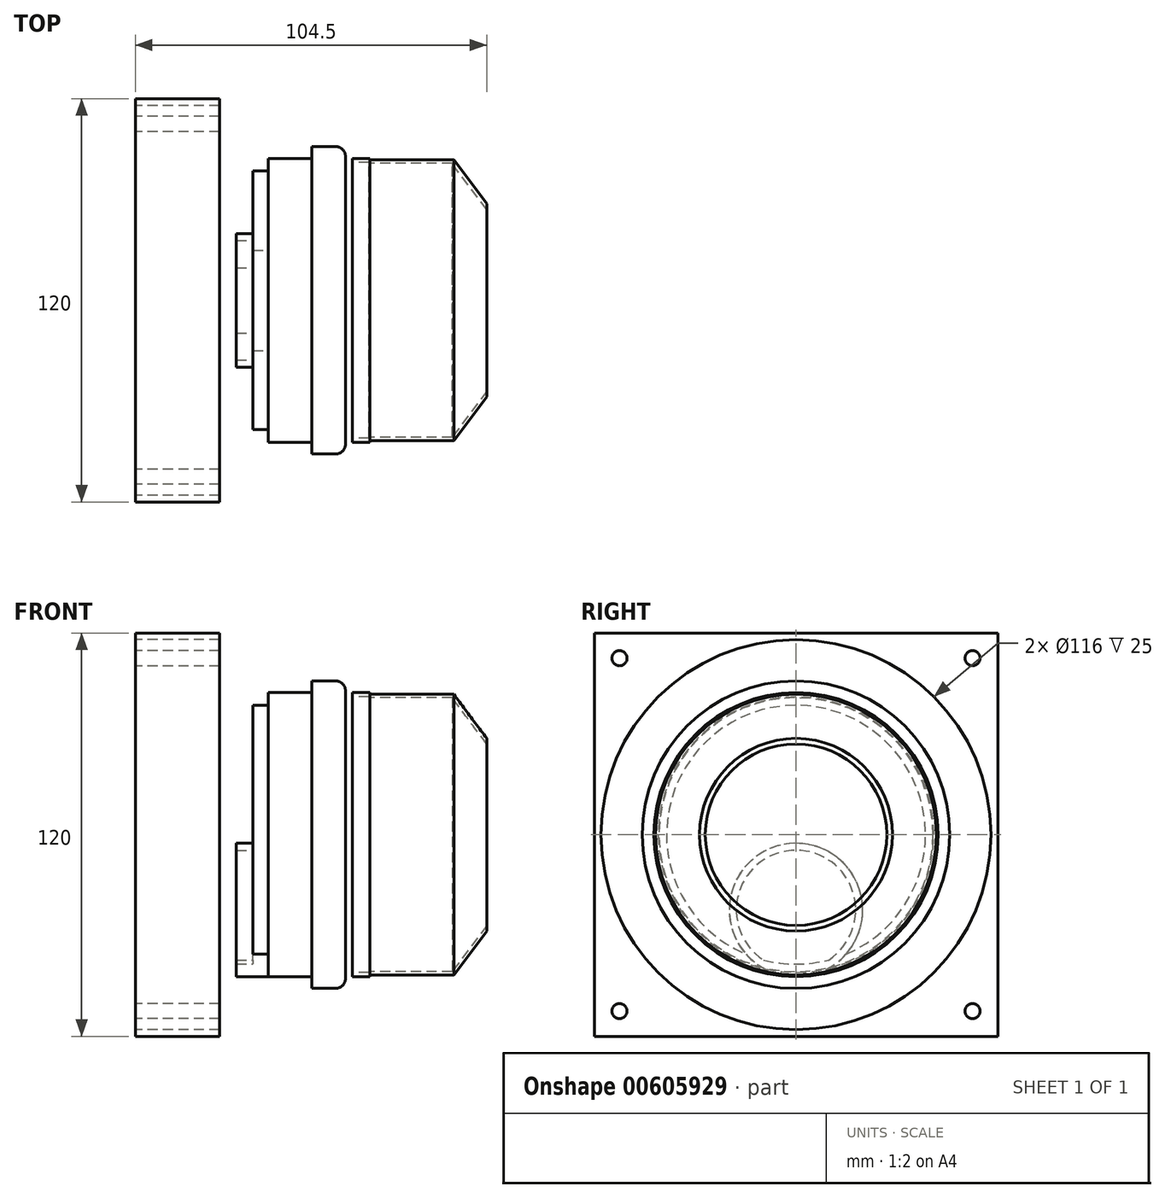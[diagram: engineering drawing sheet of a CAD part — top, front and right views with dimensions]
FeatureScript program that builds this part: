
annotation { "Feature Type Name" : "Feature", "Feature Type Description" : "" }
export const myFeature = defineFeature(function(context is Context, id is Id, definition is map)
    precondition{}
    {
        {
            var Q0;
            Q0=qCreatedBy(makeId("Top.planeOp"),FACE);
            var sketch = newSketch(context, id + "F0", { "sketchPlane" : qUnion([Q0])});
            skLineSegment(sketch, "E0.bottom", {"start": v(12.5, -60) * mm, "end": v(-12.5, -60) * mm});
            skLineSegment(sketch, "E0.top", {"start": v(12.5, 60) * mm, "end": v(-12.5, 60) * mm});
            skLineSegment(sketch, "E0.left", {"start": v(12.5, -60) * mm, "end": v(12.5, 60) * mm});
            skLineSegment(sketch, "E0.right", {"start": v(-12.5, -60) * mm, "end": v(-12.5, 60) * mm});
            skPoint(sketch, "E0.middle", {"position": v(0, 0) * mm});
            skLineSegment(sketch, "E1.bottom", {"start": v(50, -45.75) * mm, "end": v(40, -45.75) * mm});
            skLineSegment(sketch, "E1.top", {"start": v(50, 45.75) * mm, "end": v(40, 45.75) * mm});
            skLineSegment(sketch, "E1.left", {"start": v(50, -45.75) * mm, "end": v(50, 45.75) * mm});
            skLineSegment(sketch, "E1.right", {"start": v(40, -45.75) * mm, "end": v(40, 45.75) * mm});
            skPoint(sketch, "E1.middle", {"position": v(45, 0) * mm});
            skPoint(sketch, "E1.middle.positionSnap0", {"position": v(12.5, 0) * mm});
            skPoint(sketch, "E1.centerSnap0", {"position": v(12.5, 0) * mm});
            skLineSegment(sketch, "E2", {"start": v(-151.33, 0) * mm, "end": v(194.4, 0) * mm});
            skLineSegment(sketch, "E3", {"start": v(40, 42.25) * mm, "end": v(27, 42.25) * mm});
            skLineSegment(sketch, "E4", {"start": v(27, 42.25) * mm, "end": v(27, 0) * mm});
            skLineSegment(sketch, "E5.MirrorCS", {"start": v(27, -42.25) * mm, "end": v(27, 0) * mm});
            skLineSegment(sketch, "E6.MirrorCS", {"start": v(40, -42.25) * mm, "end": v(27, -42.25) * mm});
            skLineSegment(sketch, "E7", {"start": v(27, 38.5) * mm, "end": v(22.5, 38.5) * mm});
            skLineSegment(sketch, "E8", {"start": v(22.5, 38.5) * mm, "end": v(22.5, 0) * mm});
            skLineSegment(sketch, "E9.MirrorCS", {"start": v(22.5, -38.5) * mm, "end": v(22.5, 0) * mm});
            skLineSegment(sketch, "E10.MirrorCS", {"start": v(27, -38.5) * mm, "end": v(22.5, -38.5) * mm});
            skLineSegment(sketch, "E11.bottom", {"start": v(57, -41) * mm, "end": v(52, -41) * mm});
            skLineSegment(sketch, "E11.top", {"start": v(57, 41) * mm, "end": v(52, 41) * mm});
            skLineSegment(sketch, "E11.left", {"start": v(57, -41) * mm, "end": v(57, 41) * mm});
            skLineSegment(sketch, "E11.right", {"start": v(52, -41) * mm, "end": v(52, 41) * mm});
            skPoint(sketch, "E11.middle", {"position": v(54.5, 0) * mm});
            skLineSegment(sketch, "E12", {"start": v(52, -41) * mm, "end": v(52, -42.25) * mm});
            skLineSegment(sketch, "E13", {"start": v(52, -42.25) * mm, "end": v(57.2, -42.25) * mm});
            skLineSegment(sketch, "E14", {"start": v(57.2, -42.25) * mm, "end": v(57.2, -41.75) * mm});
            skLineSegment(sketch, "E15", {"start": v(57.2, -41.75) * mm, "end": v(82.2, -41.75) * mm});
            skLineSegment(sketch, "E16", {"start": v(82.2, -41.75) * mm, "end": v(92, -28.67) * mm});
            skLineSegment(sketch, "E17", {"start": v(92, -28.67) * mm, "end": v(92, -27) * mm});
            skLineSegment(sketch, "E18", {"start": v(92, -27) * mm, "end": v(81.7, -40.75) * mm});
            skLineSegment(sketch, "E19", {"start": v(81.7, -40.75) * mm, "end": v(57, -40.75) * mm});
            skLineSegment(sketch, "E20.MirrorCS", {"start": v(52, 41) * mm, "end": v(52, 42.25) * mm});
            skLineSegment(sketch, "E21.MirrorCS", {"start": v(52, 42.25) * mm, "end": v(57.2, 42.25) * mm});
            skLineSegment(sketch, "E22.MirrorCS", {"start": v(81.7, 40.75) * mm, "end": v(57, 40.75) * mm});
            skLineSegment(sketch, "E23.MirrorCS", {"start": v(57.2, 42.25) * mm, "end": v(57.2, 41.75) * mm});
            skLineSegment(sketch, "E24.MirrorCS", {"start": v(57.2, 41.75) * mm, "end": v(82.2, 41.75) * mm});
            skLineSegment(sketch, "E25.MirrorCS", {"start": v(92, 27) * mm, "end": v(81.7, 40.75) * mm});
            skLineSegment(sketch, "E26.MirrorCS", {"start": v(82.2, 41.75) * mm, "end": v(92, 28.67) * mm});
            skLineSegment(sketch, "E27.MirrorCS", {"start": v(92, 28.67) * mm, "end": v(92, 27) * mm});
            skSolve(sketch);
        }
        {
            var Q0;
            {var subQ0=sQuery(id+"F0.wireOp",EDGE,"E0.top");Q0=makeQuery(id+"F0.imprint","IMPRINT",FACE,{"disambiguationData":[TD([[makeQuery(id+"F0.imprint","IMPRINT",EDGE,{"derivedFrom":subQ0}),1.0]])]});}
            var Q1;
            {var subQ0=sQuery(id+"F0.wireOp",EDGE,"E0.bottom");Q1=makeQuery(id+"F0.imprint","IMPRINT",FACE,{"disambiguationData":[TD([[makeQuery(id+"F0.imprint","IMPRINT",EDGE,{"derivedFrom":subQ0}),-1.0]])]});}
            extrude(context, id + "F1", {"entities" : qUnion([Q0, Q1]), "endBound" : BoundingType.SYMMETRIC, "depth" : 120 * mm, "offsetDistance" : 25 * mm});
        }
        {
            var Q0;
            {var subQ4=sQuery(id+"F0.wireOp",EDGE,"E7");Q0=makeQuery(id+"F0.imprint","IMPRINT",FACE,{"disambiguationData":[TD([[makeQuery(id+"F0.imprint","IMPRINT",EDGE,{"derivedFrom":subQ4}),1.0]])]});}
            var Q1;
            {var subQ1=sQuery(id+"F0.wireOp",EDGE,"E3");Q1=makeQuery(id+"F0.imprint","IMPRINT",FACE,{"disambiguationData":[TD([[makeQuery(id+"F0.imprint","IMPRINT",EDGE,{"derivedFrom":subQ1}),1.0]])]});}
            var Q2;
            {var subQ1=sQuery(id+"F0.wireOp",EDGE,"E1.top");Q2=makeQuery(id+"F0.imprint","IMPRINT",FACE,{"disambiguationData":[TD([[makeQuery(id+"F0.imprint","IMPRINT",EDGE,{"derivedFrom":subQ1}),1.0]])]});}
            var Q3;
            {var subQ1=sQuery(id+"F0.wireOp",EDGE,"E11.top");Q3=makeQuery(id+"F0.imprint","IMPRINT",FACE,{"disambiguationData":[TD([[makeQuery(id+"F0.imprint","IMPRINT",EDGE,{"derivedFrom":subQ1}),-1.0]])]});}
            var Q4;
            Q4=sQuery(id+"F0.wireOp",EDGE,"E2");
            revolve(context, id + "F2", {"entities" : qUnion([Q0, Q1, Q2, Q3]), "axis" : qUnion([Q4]), "revolveType" : RevolveType.FULL});
        }
        {
            var Q0;
            Q0=makeQuery(id+"F2.opRevolve","SWEPT_EDGE",EDGE,{"disambiguationData":[OSD([sQuery(id+"F0.wireOp",EDGE,"E1.top"),sQuery(id+"F0.wireOp",EDGE,"E1.left")])]});
            fillet(context, id + "F3", {"entities" : qUnion([Q0]), "radius" : 3 * mm, "tangentPropagation" : true, "allowEdgeOverflow" : false});
        }
        {
            var Q0;
            Q0=makeQuery(id+"F1.opExtrude","SWEPT_FACE",FACE,{"disambiguationData":[OSD([sQuery(id+"F0.wireOp",EDGE,"E0.right")])]});
            var sketch = newSketch(context, id + "F4", { "sketchPlane" : qUnion([Q0])});
            skCircle(sketch, "E28", {"center": v(0, 0) * mm, "radius": 58 * mm});
            skCircle(sketch, "E29", {"center": v(-52.5, 52.5) * mm, "radius": 2.25 * mm});
            skLineSegment(sketch, "E30", {"start": v(0, 0) * mm, "end": v(0, -23.1) * mm, "construction": true});
            skLineSegment(sketch, "E31", {"start": v(0, 0) * mm, "end": v(-29.22, 0) * mm, "construction": true});
            skCircle(sketch, "E32.MirrorC", {"center": v(-52.5, -52.5) * mm, "radius": 2.25 * mm});
            skCircle(sketch, "E33.MirrorC", {"center": v(52.5, -52.5) * mm, "radius": 2.25 * mm});
            skCircle(sketch, "E34.MirrorC", {"center": v(52.5, 52.5) * mm, "radius": 2.25 * mm});
            skSolve(sketch);
        }
        {
            var Q0;
            Q0=qSketchRegion(id+"F4",true);
            extrude(context, id + "F5", {"entities" : qUnion([Q0]), "operationType" : NewBodyOperationType.REMOVE, "oppositeDirection" : true, "depth" : 25 * mm, "offsetDistance" : 25 * mm});
        }
        {
            var Q0;
            Q0=makeQuery(id+"F2.opRevolve","SWEPT_FACE",FACE,{"disambiguationData":[OSD([sQuery(id+"F0.wireOp",EDGE,"E8")])]});
            var sketch = newSketch(context, id + "F6", { "sketchPlane" : qUnion([Q0])});
            skCircle(sketch, "E35", {"center": v(0, -22.4) * mm, "radius": 19.85 * mm});
            skCircle(sketch, "E36", {"center": v(0, -22.4) * mm, "radius": 17.75 * mm});
            skArc(sketch, "E37", {"start": v(-9.72, -37.25) * mm, "mid": v(0, -38.5) * mm, "end": v(9.72, -37.25) * mm});
            skSolve(sketch);
        }
        {
            var Q0;
            {var subQ0=sQuery(id+"F6.wireOp",EDGE,"E35");var subQ1=makeQuery(id+"F2.opRevolve","SWEPT_EDGE",EDGE,{"disambiguationData":[OSD([sQuery(id+"F0.wireOp",EDGE,"E7"),sQuery(id+"F0.wireOp",EDGE,"E8")])]});var subQ2=makeQuery(id+"F6.imprint","INTERSECT",VERTEX,{"disambiguationData":[OD(0.0)],"derivedFrom":[subQ1,subQ0]});Q0=makeQuery(id+"F6.imprint","IMPRINT",FACE,{"disambiguationData":[TD([[makeQuery(id+"F6.imprint","IMPRINT",EDGE,{"disambiguationData":[TD([[subQ2,1.0]])],"derivedFrom":subQ0}),1.0]])]});}
            var Q1;
            {var subQ0=sQuery(id+"F6.wireOp",EDGE,"E35");var subQ1=makeQuery(id+"F2.opRevolve","SWEPT_EDGE",EDGE,{"disambiguationData":[OSD([sQuery(id+"F0.wireOp",EDGE,"E7"),sQuery(id+"F0.wireOp",EDGE,"E8")])]});var subQ2=makeQuery(id+"F6.imprint","INTERSECT",VERTEX,{"disambiguationData":[OD(0.0)],"derivedFrom":[subQ1,subQ0]});Q1=makeQuery(id+"F6.imprint","IMPRINT",FACE,{"disambiguationData":[TD([[makeQuery(id+"F6.imprint","IMPRINT",EDGE,{"disambiguationData":[TD([[subQ2,-1.0]])],"derivedFrom":subQ0}),1.0]])]});}
            var Q2;
            {var subQ0=sQuery(id+"F6.wireOp",EDGE,"E37");Q2=makeQuery(id+"F6.imprint","IMPRINT",FACE,{"disambiguationData":[TD([[makeQuery(id+"F6.imprint","IMPRINT",EDGE,{"derivedFrom":subQ0}),-1.0]])]});}
            extrude(context, id + "F7", {"entities" : qUnion([Q0, Q1, Q2]), "operationType" : NewBodyOperationType.ADD, "depth" : 5 * mm, "offsetDistance" : 25 * mm, "hasSecondDirection" : true, "secondDirectionOppositeDirection" : true, "secondDirectionDepth" : 5 * mm});
        }
    });
